# Revit family: Plumbing_Drainage_AXOR_47410600-AXOR-MyEdition-Bath-spout-47410
name_source: partatom
category: Plumbing Fixtures
revit_build: Autodesk Revit 2015 (Build: 20140606_1530(x64)
units: mm (PartAtom-declared; Revit-internal decimal feet)

## types (1)
- chrome/black glass
    BIMobject category = Drainage
    BIMobject category code = plumbing-drainage
    BIMobject main category = Plumbing
    BIMobject main category code = plumbing
    BOSUseNativeGeometries = 1
    Brand url = https://www.axor-design.com
    Default Elevation = 4' - 0"
    Design country = Germany
    EAN code = https://4059625161449
    Edition number = 1
    IFC Classification = Sanitary Terminal
    Installation instructions = https://pro.hansgrohe-int.com
    Manufacturer country = Germany
    Manufacturer name = AXOR
    Masterformat 2014 Code = 22 13 16
    Masterformat 2014 Description = Sanitary Waste and Vent Piping
    NBS Reference Code = 31-76
    NBS Reference Description = Sanitary Dispensing And Disposal Units
    OmniClass Code = 23-21 23 27
    OmniClass Description = Residential Waste Disposal Units
    Product Guid = 15d180dc-414b-4c12-8534-36597472d755
    Product SKU = 47410600
    Product data url = https://bimobject.com
    Product family = AXOR MyEdition
    Product group = Bath fillers
    Product url = https://pro.hansgrohe-int.com
    QR code = http://bimobject.com
    Technical description = https://pro.hansgrohe-int.com
    UNSPSC Code = 3018
    Uniclass 1.4 Code = L721
    Uniclass 1.4 Description = Sanitary equipment
    Uniclass 2.0 Code = PR-31-76
    Uniclass 2.0 Description = Sanitary Dispensing And Disposal Units
    Uniclass 2015 Code = Pr_60_45_90
    Uniclass 2015 Name = Wastewater and water mixer products
    Uniformat II Code = D2010
    Uniformat II Description = Plumbing Fixtures

## geometry (parser evidence)
native form markers: Blend x2, Sweep x3
no freeform markers — native parametric forms only
